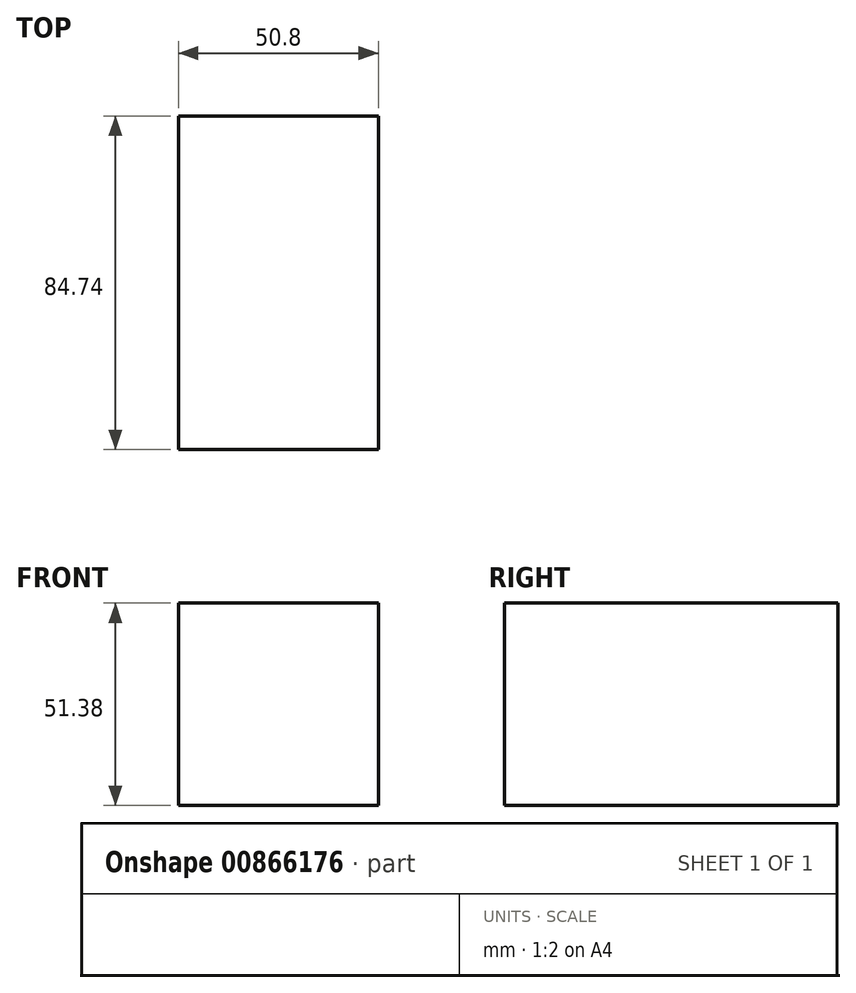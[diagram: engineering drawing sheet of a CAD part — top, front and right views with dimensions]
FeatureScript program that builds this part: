
annotation { "Feature Type Name" : "Feature", "Feature Type Description" : "" }
export const myFeature = defineFeature(function(context is Context, id is Id, definition is map)
    precondition{}
    {
        {
            var Q0;
            Q0=qCreatedBy(makeId("Right.planeOp"),FACE);
            var sketch = newSketch(context, id + "F0", { "sketchPlane" : qUnion([Q0])});
            skLineSegment(sketch, "E0.bottom", {"start": v(42.37, 25.7) * mm, "end": v(-42.37, 25.7) * mm});
            skLineSegment(sketch, "E0.top", {"start": v(42.37, -25.7) * mm, "end": v(-42.37, -25.7) * mm});
            skLineSegment(sketch, "E0.left", {"start": v(42.37, 25.7) * mm, "end": v(42.37, -25.7) * mm});
            skLineSegment(sketch, "E0.right", {"start": v(-42.37, 25.7) * mm, "end": v(-42.37, -25.7) * mm});
            skSolve(sketch);
        }
        {
            var Q0;
            Q0=makeQuery(id+"F0.imprint","IMPRINT",FACE,{"disambiguationData":[TD([[makeQuery(id+"F0.imprint","IMPRINT",EDGE,{"derivedFrom":sQuery(id+"F0.wireOp",EDGE,"E0.bottom")}),1.0]])]});
            extrude(context, id + "F1", {"entities" : qUnion([Q0]), "depth" : 25.4 * mm, "offsetDistance" : 25.4 * mm, "hasSecondDirection" : true, "secondDirectionOppositeDirection" : true, "secondDirectionDepth" : 25.4 * mm});
        }
    });
